AUTODESK INVENTOR PART (.ipt)
format: ipt  version: 2024 (Build 280153000, 153)  size: 122,880 bytes
history: native  units: mm
features: extrude x4, sketch x4, projected_geometry x2
ambient origin geometry x8: Origin, YZ Plane, XZ Plane, XY Plane, X Axis, Y Axis, Z Axis, Center Point
bodies: Solid1 (feature_tree)
feature tree (10):
  extrude  "Extrusion1"  Depth=2.0mm TaperAngle=0.0deg
  extrude  "Extrusion2"  Depth=79.5mm
  extrude  "Extrusion3"  Depth=3.0mm
  extrude  "Extrusion4"  Depth=3.0mm
  sketch  "Sketch1"  dims[d0=2.0mm d1=0.0mm d4=48.0mm d5=0.0mm]
  sketch  "Sketch2"  dims[d6=106.0mm d7=79.5mm]
  projected_geometry  "Projected Loop1"
  sketch  "Sketch3"  dims[d10=7.0mm d11=3.0mm]
  sketch  "Sketch4"  dims[d12=3.0mm d13=3.0mm d14=5.0mm d16=3.0mm d17=33.0mm d18=0.0mm d19=1.0mm d20=33.0mm d21=0.0mm d22=3.5mm]
  projected_geometry  "Projected Loop2"
